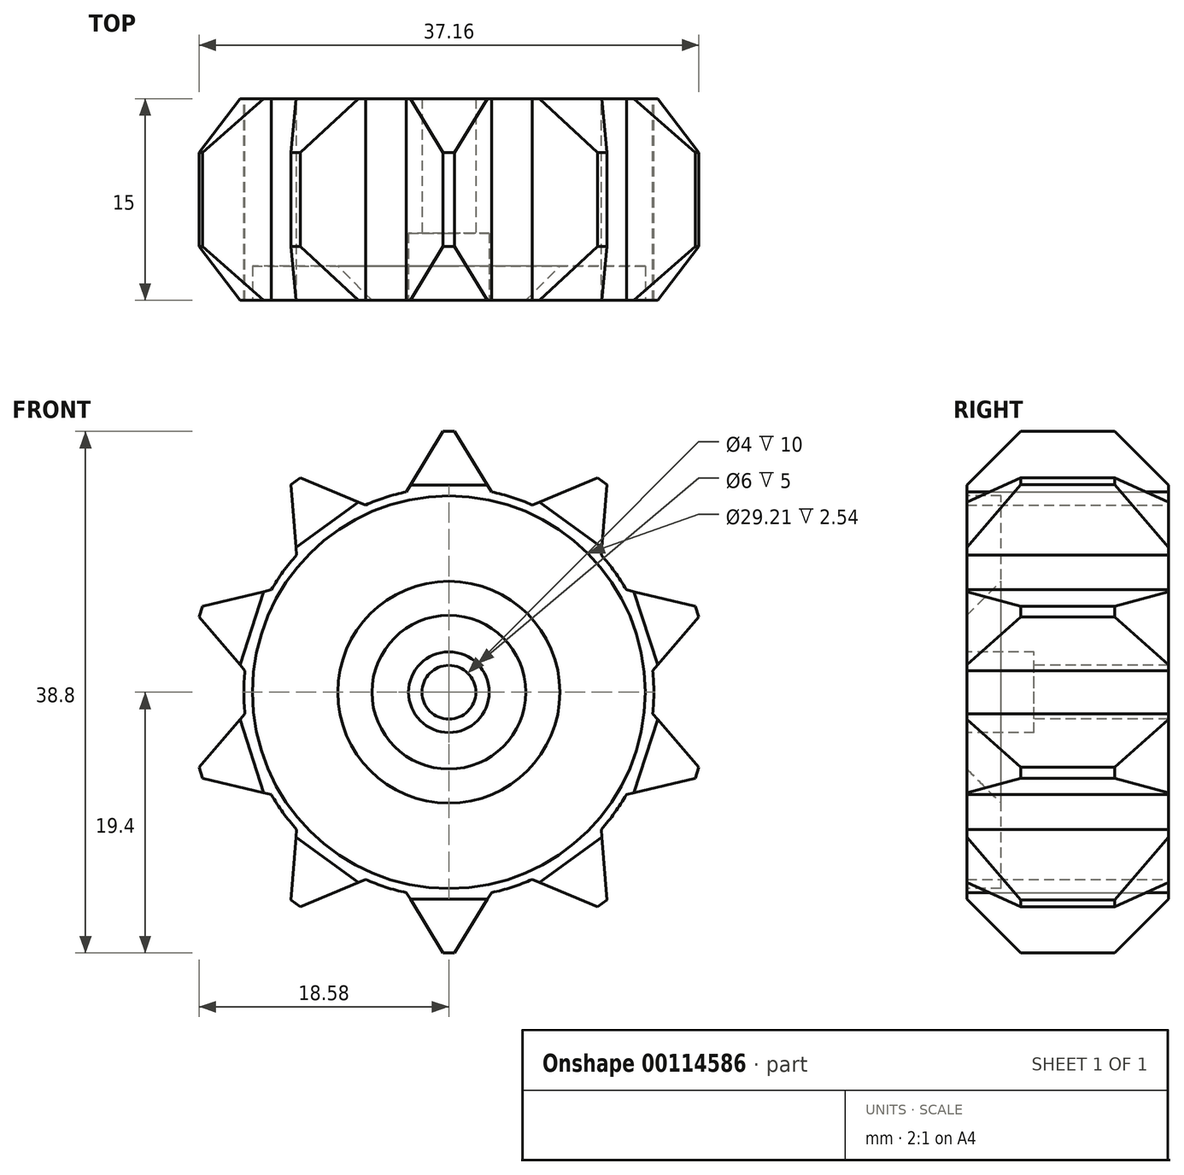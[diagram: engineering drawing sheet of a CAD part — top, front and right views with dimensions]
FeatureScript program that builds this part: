
annotation { "Feature Type Name" : "Feature", "Feature Type Description" : "" }
export const myFeature = defineFeature(function(context is Context, id is Id, definition is map)
    precondition{}
    {
        {
            var Q0;
            Q0=qCreatedBy(makeId("Front.planeOp"),FACE);
            var sketch = newSketch(context, id + "F0", { "sketchPlane" : qUnion([Q0])});
            skCircle(sketch, "E0", {"center": v(0, 0) * mm, "radius": 15.24 * mm});
            skLineSegment(sketch, "E1", {"start": v(0, 20.1) * mm, "end": v(3.17, 14.9) * mm});
            skLineSegment(sketch, "E2.MirrorCS", {"start": v(0, 20.1) * mm, "end": v(-3.17, 14.9) * mm});
            skLineSegment(sketch, "E3.1.0", {"start": v(-11.81, 16.26) * mm, "end": v(-11.32, 10.2) * mm});
            skLineSegment(sketch, "E3.1.1", {"start": v(-11.81, 16.26) * mm, "end": v(-6.2, 13.92) * mm});
            skLineSegment(sketch, "E3.2.0", {"start": v(-19.12, 6.21) * mm, "end": v(-15.16, 1.6) * mm});
            skLineSegment(sketch, "E3.2.1", {"start": v(-19.12, 6.21) * mm, "end": v(-13.2, 7.62) * mm});
            skLineSegment(sketch, "E4.2.3.0", {"start": v(-19.12, -6.21) * mm, "end": v(-13.2, -7.62) * mm});
            skLineSegment(sketch, "E4.3.3.0", {"start": v(-19.12, -6.21) * mm, "end": v(-15.16, -1.6) * mm});
            skLineSegment(sketch, "E4.2.4.0", {"start": v(-11.81, -16.26) * mm, "end": v(-6.2, -13.92) * mm});
            skLineSegment(sketch, "E4.3.4.0", {"start": v(-11.81, -16.26) * mm, "end": v(-11.32, -10.2) * mm});
            skLineSegment(sketch, "E4.2.5.0", {"start": v(0, -20.1) * mm, "end": v(3.17, -14.9) * mm});
            skLineSegment(sketch, "E4.3.5.0", {"start": v(0, -20.1) * mm, "end": v(-3.17, -14.9) * mm});
            skLineSegment(sketch, "E5.2.6.0", {"start": v(11.81, -16.26) * mm, "end": v(11.32, -10.2) * mm});
            skLineSegment(sketch, "E5.3.6.0", {"start": v(11.81, -16.26) * mm, "end": v(6.2, -13.92) * mm});
            skLineSegment(sketch, "E5.2.7.0", {"start": v(19.12, -6.21) * mm, "end": v(15.16, -1.6) * mm});
            skLineSegment(sketch, "E5.3.7.0", {"start": v(19.12, -6.21) * mm, "end": v(13.2, -7.62) * mm});
            skLineSegment(sketch, "E6.2.8.0", {"start": v(19.12, 6.21) * mm, "end": v(13.2, 7.62) * mm});
            skLineSegment(sketch, "E6.3.8.0", {"start": v(19.12, 6.21) * mm, "end": v(15.16, 1.6) * mm});
            skLineSegment(sketch, "E6.2.9.0", {"start": v(11.81, 16.26) * mm, "end": v(6.2, 13.92) * mm});
            skLineSegment(sketch, "E6.3.9.0", {"start": v(11.81, 16.26) * mm, "end": v(11.32, 10.2) * mm});
            skSolve(sketch);
        }
        {
            var Q0;
            {var subQ0=sQuery(id+"F0.wireOp",EDGE,"E4.2.5.0");Q0=makeQuery(id+"F0.imprint","IMPRINT",FACE,{"disambiguationData":[TD([[makeQuery(id+"F0.imprint","IMPRINT",EDGE,{"derivedFrom":subQ0}),1.0]])]});}
            var Q1;
            {var subQ0=sQuery(id+"F0.wireOp",EDGE,"E1");Q1=makeQuery(id+"F0.imprint","IMPRINT",FACE,{"disambiguationData":[TD([[makeQuery(id+"F0.imprint","IMPRINT",EDGE,{"derivedFrom":subQ0}),-1.0]])]});}
            var Q2;
            {var subQ0=sQuery(id+"F0.wireOp",EDGE,"E3.1.0");Q2=makeQuery(id+"F0.imprint","IMPRINT",FACE,{"disambiguationData":[TD([[makeQuery(id+"F0.imprint","IMPRINT",EDGE,{"derivedFrom":subQ0}),1.0]])]});}
            var Q3;
            {var subQ0=sQuery(id+"F0.wireOp",EDGE,"E3.2.0");Q3=makeQuery(id+"F0.imprint","IMPRINT",FACE,{"disambiguationData":[TD([[makeQuery(id+"F0.imprint","IMPRINT",EDGE,{"derivedFrom":subQ0}),1.0]])]});}
            var Q4;
            {var subQ0=sQuery(id+"F0.wireOp",EDGE,"E4.2.3.0");Q4=makeQuery(id+"F0.imprint","IMPRINT",FACE,{"disambiguationData":[TD([[makeQuery(id+"F0.imprint","IMPRINT",EDGE,{"derivedFrom":subQ0}),1.0]])]});}
            var Q5;
            {var subQ0=sQuery(id+"F0.wireOp",EDGE,"E4.2.4.0");Q5=makeQuery(id+"F0.imprint","IMPRINT",FACE,{"disambiguationData":[TD([[makeQuery(id+"F0.imprint","IMPRINT",EDGE,{"derivedFrom":subQ0}),1.0]])]});}
            var Q6;
            {var subQ0=sQuery(id+"F0.wireOp",EDGE,"E0");var subQ3=makeQuery(id+"F0.imprint","INTERSECT",VERTEX,{"derivedFrom":[subQ0,sQuery(id+"F0.wireOp",EDGE,"E4.2.5.0")]});Q6=makeQuery(id+"F0.imprint","IMPRINT",FACE,{"disambiguationData":[TD([[makeQuery(id+"F0.imprint","IMPRINT",EDGE,{"disambiguationData":[TD([[subQ3,1.0]])],"derivedFrom":subQ0}),1.0]])]});}
            var Q7;
            {var subQ0=sQuery(id+"F0.wireOp",EDGE,"E6.2.9.0");Q7=makeQuery(id+"F0.imprint","IMPRINT",FACE,{"disambiguationData":[TD([[makeQuery(id+"F0.imprint","IMPRINT",EDGE,{"derivedFrom":subQ0}),1.0]])]});}
            var Q8;
            {var subQ0=sQuery(id+"F0.wireOp",EDGE,"E6.2.8.0");Q8=makeQuery(id+"F0.imprint","IMPRINT",FACE,{"disambiguationData":[TD([[makeQuery(id+"F0.imprint","IMPRINT",EDGE,{"derivedFrom":subQ0}),1.0]])]});}
            var Q9;
            {var subQ0=sQuery(id+"F0.wireOp",EDGE,"E5.2.7.0");Q9=makeQuery(id+"F0.imprint","IMPRINT",FACE,{"disambiguationData":[TD([[makeQuery(id+"F0.imprint","IMPRINT",EDGE,{"derivedFrom":subQ0}),1.0]])]});}
            var Q10;
            {var subQ0=sQuery(id+"F0.wireOp",EDGE,"E5.2.6.0");Q10=makeQuery(id+"F0.imprint","IMPRINT",FACE,{"disambiguationData":[TD([[makeQuery(id+"F0.imprint","IMPRINT",EDGE,{"derivedFrom":subQ0}),1.0]])]});}
            extrude(context, id + "F1", {"entities" : qUnion([Q0, Q1, Q2, Q3, Q4, Q5, Q6, Q7, Q8, Q9, Q10]), "depth" : 15 * mm});
        }
        {
            var Q0;
            Q0=makeQuery(id+"F1.opExtrude","SWEPT_EDGE",EDGE,{"disambiguationData":[OSD([sQuery(id+"F0.wireOp",EDGE,"E4.2.5.0"),sQuery(id+"F0.wireOp",EDGE,"E4.3.5.0")])]});
            var Q1;
            Q1=makeQuery(id+"F1.opExtrude","SWEPT_EDGE",EDGE,{"disambiguationData":[OSD([sQuery(id+"F0.wireOp",EDGE,"E1"),sQuery(id+"F0.wireOp",EDGE,"E2.MirrorCS")])]});
            var Q2;
            Q2=makeQuery(id+"F1.opExtrude","SWEPT_EDGE",EDGE,{"disambiguationData":[OSD([sQuery(id+"F0.wireOp",EDGE,"E4.2.4.0"),sQuery(id+"F0.wireOp",EDGE,"E4.3.4.0")])]});
            var Q3;
            Q3=makeQuery(id+"F1.opExtrude","SWEPT_EDGE",EDGE,{"disambiguationData":[OSD([sQuery(id+"F0.wireOp",EDGE,"E4.2.3.0"),sQuery(id+"F0.wireOp",EDGE,"E4.3.3.0")])]});
            var Q4;
            Q4=makeQuery(id+"F1.opExtrude","SWEPT_EDGE",EDGE,{"disambiguationData":[OSD([sQuery(id+"F0.wireOp",EDGE,"E3.2.0"),sQuery(id+"F0.wireOp",EDGE,"E3.2.1")])]});
            var Q5;
            Q5=makeQuery(id+"F1.opExtrude","SWEPT_EDGE",EDGE,{"disambiguationData":[OSD([sQuery(id+"F0.wireOp",EDGE,"E3.1.0"),sQuery(id+"F0.wireOp",EDGE,"E3.1.1")])]});
            var Q6;
            Q6=makeQuery(id+"F1.opExtrude","SWEPT_EDGE",EDGE,{"disambiguationData":[OSD([sQuery(id+"F0.wireOp",EDGE,"E6.2.9.0"),sQuery(id+"F0.wireOp",EDGE,"E6.3.9.0")])]});
            var Q7;
            Q7=makeQuery(id+"F1.opExtrude","SWEPT_EDGE",EDGE,{"disambiguationData":[OSD([sQuery(id+"F0.wireOp",EDGE,"E6.2.8.0"),sQuery(id+"F0.wireOp",EDGE,"E6.3.8.0")])]});
            var Q8;
            Q8=makeQuery(id+"F1.opExtrude","SWEPT_EDGE",EDGE,{"disambiguationData":[OSD([sQuery(id+"F0.wireOp",EDGE,"E5.2.7.0"),sQuery(id+"F0.wireOp",EDGE,"E5.3.7.0")])]});
            var Q9;
            Q9=makeQuery(id+"F1.opExtrude","SWEPT_EDGE",EDGE,{"disambiguationData":[OSD([sQuery(id+"F0.wireOp",EDGE,"E5.2.6.0"),sQuery(id+"F0.wireOp",EDGE,"E5.3.6.0")])]});
            chamfer(context, id + "F2", {"entities" : qUnion([Q0, Q1, Q2, Q3, Q4, Q5, Q6, Q7, Q8, Q9]), "width" : .5 * mm, "tangentPropagation" : true});
        }
        {
            var Q0;
            {var subQ0=sQuery(id+"F0.wireOp",EDGE,"E3.1.1");var subQ1=sQuery(id+"F0.wireOp",EDGE,"E3.1.0");Q0=makeQuery(id+"F2.opChamfer","BLEND_EDGE",EDGE,{"blendedFrom":[makeQuery(id+"F1.opExtrude","SWEPT_EDGE",EDGE,{"disambiguationData":[OSD([subQ1,subQ0])]}),makeQuery(id+"F1.opExtrude","CAP_FACE",FACE,{"disambiguationData":[OSD([sQuery(id+"F0.wireOp",EDGE,"E0"),sQuery(id+"F0.wireOp",EDGE,"E1"),sQuery(id+"F0.wireOp",EDGE,"E2.MirrorCS"),subQ1,subQ0,sQuery(id+"F0.wireOp",EDGE,"E3.2.0"),sQuery(id+"F0.wireOp",EDGE,"E3.2.1"),sQuery(id+"F0.wireOp",EDGE,"E4.2.3.0"),sQuery(id+"F0.wireOp",EDGE,"E4.3.3.0"),sQuery(id+"F0.wireOp",EDGE,"E4.2.4.0"),sQuery(id+"F0.wireOp",EDGE,"E4.3.4.0"),sQuery(id+"F0.wireOp",EDGE,"E4.2.5.0"),sQuery(id+"F0.wireOp",EDGE,"E4.3.5.0")])],"isStart":false})],"blendedInto":[makeQuery(id+"F1.opExtrude","CAP_FACE",FACE,{"disambiguationData":[OSD([sQuery(id+"F0.wireOp",EDGE,"E0"),sQuery(id+"F0.wireOp",EDGE,"E1"),sQuery(id+"F0.wireOp",EDGE,"E2.MirrorCS"),subQ1,subQ0,sQuery(id+"F0.wireOp",EDGE,"E3.2.0"),sQuery(id+"F0.wireOp",EDGE,"E3.2.1"),sQuery(id+"F0.wireOp",EDGE,"E4.2.3.0"),sQuery(id+"F0.wireOp",EDGE,"E4.3.3.0"),sQuery(id+"F0.wireOp",EDGE,"E4.2.4.0"),sQuery(id+"F0.wireOp",EDGE,"E4.3.4.0"),sQuery(id+"F0.wireOp",EDGE,"E4.2.5.0"),sQuery(id+"F0.wireOp",EDGE,"E4.3.5.0")])],"isStart":false})]});}
            var Q1;
            {var subQ0=sQuery(id+"F0.wireOp",EDGE,"E3.1.1");var subQ1=sQuery(id+"F0.wireOp",EDGE,"E3.1.0");Q1=makeQuery(id+"F2.opChamfer","BLEND_EDGE",EDGE,{"blendedFrom":[makeQuery(id+"F1.opExtrude","SWEPT_EDGE",EDGE,{"disambiguationData":[OSD([subQ1,subQ0])]}),makeQuery(id+"F1.opExtrude","CAP_FACE",FACE,{"disambiguationData":[OSD([sQuery(id+"F0.wireOp",EDGE,"E0"),sQuery(id+"F0.wireOp",EDGE,"E1"),sQuery(id+"F0.wireOp",EDGE,"E2.MirrorCS"),subQ1,subQ0,sQuery(id+"F0.wireOp",EDGE,"E3.2.0"),sQuery(id+"F0.wireOp",EDGE,"E3.2.1"),sQuery(id+"F0.wireOp",EDGE,"E4.2.3.0"),sQuery(id+"F0.wireOp",EDGE,"E4.3.3.0"),sQuery(id+"F0.wireOp",EDGE,"E4.2.4.0"),sQuery(id+"F0.wireOp",EDGE,"E4.3.4.0"),sQuery(id+"F0.wireOp",EDGE,"E4.2.5.0"),sQuery(id+"F0.wireOp",EDGE,"E4.3.5.0")])],"isStart":true})],"blendedInto":[makeQuery(id+"F1.opExtrude","CAP_FACE",FACE,{"disambiguationData":[OSD([sQuery(id+"F0.wireOp",EDGE,"E0"),sQuery(id+"F0.wireOp",EDGE,"E1"),sQuery(id+"F0.wireOp",EDGE,"E2.MirrorCS"),subQ1,subQ0,sQuery(id+"F0.wireOp",EDGE,"E3.2.0"),sQuery(id+"F0.wireOp",EDGE,"E3.2.1"),sQuery(id+"F0.wireOp",EDGE,"E4.2.3.0"),sQuery(id+"F0.wireOp",EDGE,"E4.3.3.0"),sQuery(id+"F0.wireOp",EDGE,"E4.2.4.0"),sQuery(id+"F0.wireOp",EDGE,"E4.3.4.0"),sQuery(id+"F0.wireOp",EDGE,"E4.2.5.0"),sQuery(id+"F0.wireOp",EDGE,"E4.3.5.0")])],"isStart":true})]});}
            var Q2;
            {var subQ0=sQuery(id+"F0.wireOp",EDGE,"E2.MirrorCS");var subQ1=sQuery(id+"F0.wireOp",EDGE,"E1");Q2=makeQuery(id+"F2.opChamfer","BLEND_EDGE",EDGE,{"blendedFrom":[makeQuery(id+"F1.opExtrude","SWEPT_EDGE",EDGE,{"disambiguationData":[OSD([subQ1,subQ0])]}),makeQuery(id+"F1.opExtrude","CAP_FACE",FACE,{"disambiguationData":[OSD([sQuery(id+"F0.wireOp",EDGE,"E0"),subQ1,subQ0,sQuery(id+"F0.wireOp",EDGE,"E3.1.0"),sQuery(id+"F0.wireOp",EDGE,"E3.1.1"),sQuery(id+"F0.wireOp",EDGE,"E3.2.0"),sQuery(id+"F0.wireOp",EDGE,"E3.2.1"),sQuery(id+"F0.wireOp",EDGE,"E4.2.3.0"),sQuery(id+"F0.wireOp",EDGE,"E4.3.3.0"),sQuery(id+"F0.wireOp",EDGE,"E4.2.4.0"),sQuery(id+"F0.wireOp",EDGE,"E4.3.4.0"),sQuery(id+"F0.wireOp",EDGE,"E4.2.5.0"),sQuery(id+"F0.wireOp",EDGE,"E4.3.5.0")])],"isStart":true})],"blendedInto":[makeQuery(id+"F1.opExtrude","CAP_FACE",FACE,{"disambiguationData":[OSD([sQuery(id+"F0.wireOp",EDGE,"E0"),subQ1,subQ0,sQuery(id+"F0.wireOp",EDGE,"E3.1.0"),sQuery(id+"F0.wireOp",EDGE,"E3.1.1"),sQuery(id+"F0.wireOp",EDGE,"E3.2.0"),sQuery(id+"F0.wireOp",EDGE,"E3.2.1"),sQuery(id+"F0.wireOp",EDGE,"E4.2.3.0"),sQuery(id+"F0.wireOp",EDGE,"E4.3.3.0"),sQuery(id+"F0.wireOp",EDGE,"E4.2.4.0"),sQuery(id+"F0.wireOp",EDGE,"E4.3.4.0"),sQuery(id+"F0.wireOp",EDGE,"E4.2.5.0"),sQuery(id+"F0.wireOp",EDGE,"E4.3.5.0")])],"isStart":true})]});}
            var Q3;
            {var subQ0=sQuery(id+"F0.wireOp",EDGE,"E2.MirrorCS");var subQ1=sQuery(id+"F0.wireOp",EDGE,"E1");Q3=makeQuery(id+"F2.opChamfer","BLEND_EDGE",EDGE,{"blendedFrom":[makeQuery(id+"F1.opExtrude","SWEPT_EDGE",EDGE,{"disambiguationData":[OSD([subQ1,subQ0])]}),makeQuery(id+"F1.opExtrude","CAP_FACE",FACE,{"disambiguationData":[OSD([sQuery(id+"F0.wireOp",EDGE,"E0"),subQ1,subQ0,sQuery(id+"F0.wireOp",EDGE,"E3.1.0"),sQuery(id+"F0.wireOp",EDGE,"E3.1.1"),sQuery(id+"F0.wireOp",EDGE,"E3.2.0"),sQuery(id+"F0.wireOp",EDGE,"E3.2.1"),sQuery(id+"F0.wireOp",EDGE,"E4.2.3.0"),sQuery(id+"F0.wireOp",EDGE,"E4.3.3.0"),sQuery(id+"F0.wireOp",EDGE,"E4.2.4.0"),sQuery(id+"F0.wireOp",EDGE,"E4.3.4.0"),sQuery(id+"F0.wireOp",EDGE,"E4.2.5.0"),sQuery(id+"F0.wireOp",EDGE,"E4.3.5.0")])],"isStart":false})],"blendedInto":[makeQuery(id+"F1.opExtrude","CAP_FACE",FACE,{"disambiguationData":[OSD([sQuery(id+"F0.wireOp",EDGE,"E0"),subQ1,subQ0,sQuery(id+"F0.wireOp",EDGE,"E3.1.0"),sQuery(id+"F0.wireOp",EDGE,"E3.1.1"),sQuery(id+"F0.wireOp",EDGE,"E3.2.0"),sQuery(id+"F0.wireOp",EDGE,"E3.2.1"),sQuery(id+"F0.wireOp",EDGE,"E4.2.3.0"),sQuery(id+"F0.wireOp",EDGE,"E4.3.3.0"),sQuery(id+"F0.wireOp",EDGE,"E4.2.4.0"),sQuery(id+"F0.wireOp",EDGE,"E4.3.4.0"),sQuery(id+"F0.wireOp",EDGE,"E4.2.5.0"),sQuery(id+"F0.wireOp",EDGE,"E4.3.5.0")])],"isStart":false})]});}
            var Q4;
            {var subQ0=sQuery(id+"F0.wireOp",EDGE,"E4.3.5.0");var subQ1=sQuery(id+"F0.wireOp",EDGE,"E4.2.5.0");Q4=makeQuery(id+"F2.opChamfer","BLEND_EDGE",EDGE,{"blendedFrom":[makeQuery(id+"F1.opExtrude","SWEPT_EDGE",EDGE,{"disambiguationData":[OSD([subQ1,subQ0])]}),makeQuery(id+"F1.opExtrude","CAP_FACE",FACE,{"disambiguationData":[OSD([sQuery(id+"F0.wireOp",EDGE,"E0"),sQuery(id+"F0.wireOp",EDGE,"E1"),sQuery(id+"F0.wireOp",EDGE,"E2.MirrorCS"),sQuery(id+"F0.wireOp",EDGE,"E3.1.0"),sQuery(id+"F0.wireOp",EDGE,"E3.1.1"),sQuery(id+"F0.wireOp",EDGE,"E3.2.0"),sQuery(id+"F0.wireOp",EDGE,"E3.2.1"),sQuery(id+"F0.wireOp",EDGE,"E4.2.3.0"),sQuery(id+"F0.wireOp",EDGE,"E4.3.3.0"),sQuery(id+"F0.wireOp",EDGE,"E4.2.4.0"),sQuery(id+"F0.wireOp",EDGE,"E4.3.4.0"),subQ1,subQ0])],"isStart":false})],"blendedInto":[makeQuery(id+"F1.opExtrude","CAP_FACE",FACE,{"disambiguationData":[OSD([sQuery(id+"F0.wireOp",EDGE,"E0"),sQuery(id+"F0.wireOp",EDGE,"E1"),sQuery(id+"F0.wireOp",EDGE,"E2.MirrorCS"),sQuery(id+"F0.wireOp",EDGE,"E3.1.0"),sQuery(id+"F0.wireOp",EDGE,"E3.1.1"),sQuery(id+"F0.wireOp",EDGE,"E3.2.0"),sQuery(id+"F0.wireOp",EDGE,"E3.2.1"),sQuery(id+"F0.wireOp",EDGE,"E4.2.3.0"),sQuery(id+"F0.wireOp",EDGE,"E4.3.3.0"),sQuery(id+"F0.wireOp",EDGE,"E4.2.4.0"),sQuery(id+"F0.wireOp",EDGE,"E4.3.4.0"),subQ1,subQ0])],"isStart":false})]});}
            var Q5;
            {var subQ0=sQuery(id+"F0.wireOp",EDGE,"E4.3.4.0");var subQ1=sQuery(id+"F0.wireOp",EDGE,"E4.2.4.0");Q5=makeQuery(id+"F2.opChamfer","BLEND_EDGE",EDGE,{"blendedFrom":[makeQuery(id+"F1.opExtrude","SWEPT_EDGE",EDGE,{"disambiguationData":[OSD([subQ1,subQ0])]}),makeQuery(id+"F1.opExtrude","CAP_FACE",FACE,{"disambiguationData":[OSD([sQuery(id+"F0.wireOp",EDGE,"E0"),sQuery(id+"F0.wireOp",EDGE,"E1"),sQuery(id+"F0.wireOp",EDGE,"E2.MirrorCS"),sQuery(id+"F0.wireOp",EDGE,"E3.1.0"),sQuery(id+"F0.wireOp",EDGE,"E3.1.1"),sQuery(id+"F0.wireOp",EDGE,"E3.2.0"),sQuery(id+"F0.wireOp",EDGE,"E3.2.1"),sQuery(id+"F0.wireOp",EDGE,"E4.2.3.0"),sQuery(id+"F0.wireOp",EDGE,"E4.3.3.0"),subQ1,subQ0,sQuery(id+"F0.wireOp",EDGE,"E4.2.5.0"),sQuery(id+"F0.wireOp",EDGE,"E4.3.5.0")])],"isStart":false})],"blendedInto":[makeQuery(id+"F1.opExtrude","CAP_FACE",FACE,{"disambiguationData":[OSD([sQuery(id+"F0.wireOp",EDGE,"E0"),sQuery(id+"F0.wireOp",EDGE,"E1"),sQuery(id+"F0.wireOp",EDGE,"E2.MirrorCS"),sQuery(id+"F0.wireOp",EDGE,"E3.1.0"),sQuery(id+"F0.wireOp",EDGE,"E3.1.1"),sQuery(id+"F0.wireOp",EDGE,"E3.2.0"),sQuery(id+"F0.wireOp",EDGE,"E3.2.1"),sQuery(id+"F0.wireOp",EDGE,"E4.2.3.0"),sQuery(id+"F0.wireOp",EDGE,"E4.3.3.0"),subQ1,subQ0,sQuery(id+"F0.wireOp",EDGE,"E4.2.5.0"),sQuery(id+"F0.wireOp",EDGE,"E4.3.5.0")])],"isStart":false})]});}
            var Q6;
            {var subQ0=sQuery(id+"F0.wireOp",EDGE,"E4.3.3.0");var subQ1=sQuery(id+"F0.wireOp",EDGE,"E4.2.3.0");Q6=makeQuery(id+"F2.opChamfer","BLEND_EDGE",EDGE,{"blendedFrom":[makeQuery(id+"F1.opExtrude","SWEPT_EDGE",EDGE,{"disambiguationData":[OSD([subQ1,subQ0])]}),makeQuery(id+"F1.opExtrude","CAP_FACE",FACE,{"disambiguationData":[OSD([sQuery(id+"F0.wireOp",EDGE,"E0"),sQuery(id+"F0.wireOp",EDGE,"E1"),sQuery(id+"F0.wireOp",EDGE,"E2.MirrorCS"),sQuery(id+"F0.wireOp",EDGE,"E3.1.0"),sQuery(id+"F0.wireOp",EDGE,"E3.1.1"),sQuery(id+"F0.wireOp",EDGE,"E3.2.0"),sQuery(id+"F0.wireOp",EDGE,"E3.2.1"),subQ1,subQ0,sQuery(id+"F0.wireOp",EDGE,"E4.2.4.0"),sQuery(id+"F0.wireOp",EDGE,"E4.3.4.0"),sQuery(id+"F0.wireOp",EDGE,"E4.2.5.0"),sQuery(id+"F0.wireOp",EDGE,"E4.3.5.0")])],"isStart":false})],"blendedInto":[makeQuery(id+"F1.opExtrude","CAP_FACE",FACE,{"disambiguationData":[OSD([sQuery(id+"F0.wireOp",EDGE,"E0"),sQuery(id+"F0.wireOp",EDGE,"E1"),sQuery(id+"F0.wireOp",EDGE,"E2.MirrorCS"),sQuery(id+"F0.wireOp",EDGE,"E3.1.0"),sQuery(id+"F0.wireOp",EDGE,"E3.1.1"),sQuery(id+"F0.wireOp",EDGE,"E3.2.0"),sQuery(id+"F0.wireOp",EDGE,"E3.2.1"),subQ1,subQ0,sQuery(id+"F0.wireOp",EDGE,"E4.2.4.0"),sQuery(id+"F0.wireOp",EDGE,"E4.3.4.0"),sQuery(id+"F0.wireOp",EDGE,"E4.2.5.0"),sQuery(id+"F0.wireOp",EDGE,"E4.3.5.0")])],"isStart":false})]});}
            var Q7;
            {var subQ0=sQuery(id+"F0.wireOp",EDGE,"E3.2.1");var subQ1=sQuery(id+"F0.wireOp",EDGE,"E3.2.0");Q7=makeQuery(id+"F2.opChamfer","BLEND_EDGE",EDGE,{"blendedFrom":[makeQuery(id+"F1.opExtrude","SWEPT_EDGE",EDGE,{"disambiguationData":[OSD([subQ1,subQ0])]}),makeQuery(id+"F1.opExtrude","CAP_FACE",FACE,{"disambiguationData":[OSD([sQuery(id+"F0.wireOp",EDGE,"E0"),sQuery(id+"F0.wireOp",EDGE,"E1"),sQuery(id+"F0.wireOp",EDGE,"E2.MirrorCS"),sQuery(id+"F0.wireOp",EDGE,"E3.1.0"),sQuery(id+"F0.wireOp",EDGE,"E3.1.1"),subQ1,subQ0,sQuery(id+"F0.wireOp",EDGE,"E4.2.3.0"),sQuery(id+"F0.wireOp",EDGE,"E4.3.3.0"),sQuery(id+"F0.wireOp",EDGE,"E4.2.4.0"),sQuery(id+"F0.wireOp",EDGE,"E4.3.4.0"),sQuery(id+"F0.wireOp",EDGE,"E4.2.5.0"),sQuery(id+"F0.wireOp",EDGE,"E4.3.5.0")])],"isStart":false})],"blendedInto":[makeQuery(id+"F1.opExtrude","CAP_FACE",FACE,{"disambiguationData":[OSD([sQuery(id+"F0.wireOp",EDGE,"E0"),sQuery(id+"F0.wireOp",EDGE,"E1"),sQuery(id+"F0.wireOp",EDGE,"E2.MirrorCS"),sQuery(id+"F0.wireOp",EDGE,"E3.1.0"),sQuery(id+"F0.wireOp",EDGE,"E3.1.1"),subQ1,subQ0,sQuery(id+"F0.wireOp",EDGE,"E4.2.3.0"),sQuery(id+"F0.wireOp",EDGE,"E4.3.3.0"),sQuery(id+"F0.wireOp",EDGE,"E4.2.4.0"),sQuery(id+"F0.wireOp",EDGE,"E4.3.4.0"),sQuery(id+"F0.wireOp",EDGE,"E4.2.5.0"),sQuery(id+"F0.wireOp",EDGE,"E4.3.5.0")])],"isStart":false})]});}
            var Q8;
            {var subQ0=sQuery(id+"F0.wireOp",EDGE,"E3.2.1");var subQ1=sQuery(id+"F0.wireOp",EDGE,"E3.2.0");Q8=makeQuery(id+"F2.opChamfer","BLEND_EDGE",EDGE,{"blendedFrom":[makeQuery(id+"F1.opExtrude","SWEPT_EDGE",EDGE,{"disambiguationData":[OSD([subQ1,subQ0])]}),makeQuery(id+"F1.opExtrude","CAP_FACE",FACE,{"disambiguationData":[OSD([sQuery(id+"F0.wireOp",EDGE,"E0"),sQuery(id+"F0.wireOp",EDGE,"E1"),sQuery(id+"F0.wireOp",EDGE,"E2.MirrorCS"),sQuery(id+"F0.wireOp",EDGE,"E3.1.0"),sQuery(id+"F0.wireOp",EDGE,"E3.1.1"),subQ1,subQ0,sQuery(id+"F0.wireOp",EDGE,"E4.2.3.0"),sQuery(id+"F0.wireOp",EDGE,"E4.3.3.0"),sQuery(id+"F0.wireOp",EDGE,"E4.2.4.0"),sQuery(id+"F0.wireOp",EDGE,"E4.3.4.0"),sQuery(id+"F0.wireOp",EDGE,"E4.2.5.0"),sQuery(id+"F0.wireOp",EDGE,"E4.3.5.0")])],"isStart":true})],"blendedInto":[makeQuery(id+"F1.opExtrude","CAP_FACE",FACE,{"disambiguationData":[OSD([sQuery(id+"F0.wireOp",EDGE,"E0"),sQuery(id+"F0.wireOp",EDGE,"E1"),sQuery(id+"F0.wireOp",EDGE,"E2.MirrorCS"),sQuery(id+"F0.wireOp",EDGE,"E3.1.0"),sQuery(id+"F0.wireOp",EDGE,"E3.1.1"),subQ1,subQ0,sQuery(id+"F0.wireOp",EDGE,"E4.2.3.0"),sQuery(id+"F0.wireOp",EDGE,"E4.3.3.0"),sQuery(id+"F0.wireOp",EDGE,"E4.2.4.0"),sQuery(id+"F0.wireOp",EDGE,"E4.3.4.0"),sQuery(id+"F0.wireOp",EDGE,"E4.2.5.0"),sQuery(id+"F0.wireOp",EDGE,"E4.3.5.0")])],"isStart":true})]});}
            var Q9;
            {var subQ0=sQuery(id+"F0.wireOp",EDGE,"E4.3.3.0");var subQ1=sQuery(id+"F0.wireOp",EDGE,"E4.2.3.0");Q9=makeQuery(id+"F2.opChamfer","BLEND_EDGE",EDGE,{"blendedFrom":[makeQuery(id+"F1.opExtrude","SWEPT_EDGE",EDGE,{"disambiguationData":[OSD([subQ1,subQ0])]}),makeQuery(id+"F1.opExtrude","CAP_FACE",FACE,{"disambiguationData":[OSD([sQuery(id+"F0.wireOp",EDGE,"E0"),sQuery(id+"F0.wireOp",EDGE,"E1"),sQuery(id+"F0.wireOp",EDGE,"E2.MirrorCS"),sQuery(id+"F0.wireOp",EDGE,"E3.1.0"),sQuery(id+"F0.wireOp",EDGE,"E3.1.1"),sQuery(id+"F0.wireOp",EDGE,"E3.2.0"),sQuery(id+"F0.wireOp",EDGE,"E3.2.1"),subQ1,subQ0,sQuery(id+"F0.wireOp",EDGE,"E4.2.4.0"),sQuery(id+"F0.wireOp",EDGE,"E4.3.4.0"),sQuery(id+"F0.wireOp",EDGE,"E4.2.5.0"),sQuery(id+"F0.wireOp",EDGE,"E4.3.5.0")])],"isStart":true})],"blendedInto":[makeQuery(id+"F1.opExtrude","CAP_FACE",FACE,{"disambiguationData":[OSD([sQuery(id+"F0.wireOp",EDGE,"E0"),sQuery(id+"F0.wireOp",EDGE,"E1"),sQuery(id+"F0.wireOp",EDGE,"E2.MirrorCS"),sQuery(id+"F0.wireOp",EDGE,"E3.1.0"),sQuery(id+"F0.wireOp",EDGE,"E3.1.1"),sQuery(id+"F0.wireOp",EDGE,"E3.2.0"),sQuery(id+"F0.wireOp",EDGE,"E3.2.1"),subQ1,subQ0,sQuery(id+"F0.wireOp",EDGE,"E4.2.4.0"),sQuery(id+"F0.wireOp",EDGE,"E4.3.4.0"),sQuery(id+"F0.wireOp",EDGE,"E4.2.5.0"),sQuery(id+"F0.wireOp",EDGE,"E4.3.5.0")])],"isStart":true})]});}
            var Q10;
            {var subQ0=sQuery(id+"F0.wireOp",EDGE,"E4.3.4.0");var subQ1=sQuery(id+"F0.wireOp",EDGE,"E4.2.4.0");Q10=makeQuery(id+"F2.opChamfer","BLEND_EDGE",EDGE,{"blendedFrom":[makeQuery(id+"F1.opExtrude","SWEPT_EDGE",EDGE,{"disambiguationData":[OSD([subQ1,subQ0])]}),makeQuery(id+"F1.opExtrude","CAP_FACE",FACE,{"disambiguationData":[OSD([sQuery(id+"F0.wireOp",EDGE,"E0"),sQuery(id+"F0.wireOp",EDGE,"E1"),sQuery(id+"F0.wireOp",EDGE,"E2.MirrorCS"),sQuery(id+"F0.wireOp",EDGE,"E3.1.0"),sQuery(id+"F0.wireOp",EDGE,"E3.1.1"),sQuery(id+"F0.wireOp",EDGE,"E3.2.0"),sQuery(id+"F0.wireOp",EDGE,"E3.2.1"),sQuery(id+"F0.wireOp",EDGE,"E4.2.3.0"),sQuery(id+"F0.wireOp",EDGE,"E4.3.3.0"),subQ1,subQ0,sQuery(id+"F0.wireOp",EDGE,"E4.2.5.0"),sQuery(id+"F0.wireOp",EDGE,"E4.3.5.0")])],"isStart":true})],"blendedInto":[makeQuery(id+"F1.opExtrude","CAP_FACE",FACE,{"disambiguationData":[OSD([sQuery(id+"F0.wireOp",EDGE,"E0"),sQuery(id+"F0.wireOp",EDGE,"E1"),sQuery(id+"F0.wireOp",EDGE,"E2.MirrorCS"),sQuery(id+"F0.wireOp",EDGE,"E3.1.0"),sQuery(id+"F0.wireOp",EDGE,"E3.1.1"),sQuery(id+"F0.wireOp",EDGE,"E3.2.0"),sQuery(id+"F0.wireOp",EDGE,"E3.2.1"),sQuery(id+"F0.wireOp",EDGE,"E4.2.3.0"),sQuery(id+"F0.wireOp",EDGE,"E4.3.3.0"),subQ1,subQ0,sQuery(id+"F0.wireOp",EDGE,"E4.2.5.0"),sQuery(id+"F0.wireOp",EDGE,"E4.3.5.0")])],"isStart":true})]});}
            var Q11;
            {var subQ0=sQuery(id+"F0.wireOp",EDGE,"E4.3.5.0");var subQ1=sQuery(id+"F0.wireOp",EDGE,"E4.2.5.0");Q11=makeQuery(id+"F2.opChamfer","BLEND_EDGE",EDGE,{"blendedFrom":[makeQuery(id+"F1.opExtrude","SWEPT_EDGE",EDGE,{"disambiguationData":[OSD([subQ1,subQ0])]}),makeQuery(id+"F1.opExtrude","CAP_FACE",FACE,{"disambiguationData":[OSD([sQuery(id+"F0.wireOp",EDGE,"E0"),sQuery(id+"F0.wireOp",EDGE,"E1"),sQuery(id+"F0.wireOp",EDGE,"E2.MirrorCS"),sQuery(id+"F0.wireOp",EDGE,"E3.1.0"),sQuery(id+"F0.wireOp",EDGE,"E3.1.1"),sQuery(id+"F0.wireOp",EDGE,"E3.2.0"),sQuery(id+"F0.wireOp",EDGE,"E3.2.1"),sQuery(id+"F0.wireOp",EDGE,"E4.2.3.0"),sQuery(id+"F0.wireOp",EDGE,"E4.3.3.0"),sQuery(id+"F0.wireOp",EDGE,"E4.2.4.0"),sQuery(id+"F0.wireOp",EDGE,"E4.3.4.0"),subQ1,subQ0])],"isStart":true})],"blendedInto":[makeQuery(id+"F1.opExtrude","CAP_FACE",FACE,{"disambiguationData":[OSD([sQuery(id+"F0.wireOp",EDGE,"E0"),sQuery(id+"F0.wireOp",EDGE,"E1"),sQuery(id+"F0.wireOp",EDGE,"E2.MirrorCS"),sQuery(id+"F0.wireOp",EDGE,"E3.1.0"),sQuery(id+"F0.wireOp",EDGE,"E3.1.1"),sQuery(id+"F0.wireOp",EDGE,"E3.2.0"),sQuery(id+"F0.wireOp",EDGE,"E3.2.1"),sQuery(id+"F0.wireOp",EDGE,"E4.2.3.0"),sQuery(id+"F0.wireOp",EDGE,"E4.3.3.0"),sQuery(id+"F0.wireOp",EDGE,"E4.2.4.0"),sQuery(id+"F0.wireOp",EDGE,"E4.3.4.0"),subQ1,subQ0])],"isStart":true})]});}
            var Q12;
            {var subQ0=sQuery(id+"F0.wireOp",EDGE,"E6.3.9.0");var subQ1=sQuery(id+"F0.wireOp",EDGE,"E6.2.9.0");Q12=makeQuery(id+"F2.opChamfer","BLEND_EDGE",EDGE,{"blendedFrom":[makeQuery(id+"F1.opExtrude","SWEPT_EDGE",EDGE,{"disambiguationData":[OSD([subQ1,subQ0])]}),makeQuery(id+"F1.opExtrude","CAP_FACE",FACE,{"disambiguationData":[OSD([sQuery(id+"F0.wireOp",EDGE,"E0"),sQuery(id+"F0.wireOp",EDGE,"E1"),sQuery(id+"F0.wireOp",EDGE,"E2.MirrorCS"),sQuery(id+"F0.wireOp",EDGE,"E3.1.0"),sQuery(id+"F0.wireOp",EDGE,"E3.1.1"),sQuery(id+"F0.wireOp",EDGE,"E3.2.0"),sQuery(id+"F0.wireOp",EDGE,"E3.2.1"),sQuery(id+"F0.wireOp",EDGE,"E4.2.3.0"),sQuery(id+"F0.wireOp",EDGE,"E4.3.3.0"),sQuery(id+"F0.wireOp",EDGE,"E4.2.4.0"),sQuery(id+"F0.wireOp",EDGE,"E4.3.4.0"),sQuery(id+"F0.wireOp",EDGE,"E4.2.5.0"),sQuery(id+"F0.wireOp",EDGE,"E4.3.5.0"),sQuery(id+"F0.wireOp",EDGE,"E5.2.6.0"),sQuery(id+"F0.wireOp",EDGE,"E5.3.6.0"),sQuery(id+"F0.wireOp",EDGE,"E5.2.7.0"),sQuery(id+"F0.wireOp",EDGE,"E5.3.7.0"),sQuery(id+"F0.wireOp",EDGE,"E6.2.8.0"),sQuery(id+"F0.wireOp",EDGE,"E6.3.8.0"),subQ1,subQ0])],"isStart":false})],"blendedInto":[makeQuery(id+"F1.opExtrude","CAP_FACE",FACE,{"disambiguationData":[OSD([sQuery(id+"F0.wireOp",EDGE,"E0"),sQuery(id+"F0.wireOp",EDGE,"E1"),sQuery(id+"F0.wireOp",EDGE,"E2.MirrorCS"),sQuery(id+"F0.wireOp",EDGE,"E3.1.0"),sQuery(id+"F0.wireOp",EDGE,"E3.1.1"),sQuery(id+"F0.wireOp",EDGE,"E3.2.0"),sQuery(id+"F0.wireOp",EDGE,"E3.2.1"),sQuery(id+"F0.wireOp",EDGE,"E4.2.3.0"),sQuery(id+"F0.wireOp",EDGE,"E4.3.3.0"),sQuery(id+"F0.wireOp",EDGE,"E4.2.4.0"),sQuery(id+"F0.wireOp",EDGE,"E4.3.4.0"),sQuery(id+"F0.wireOp",EDGE,"E4.2.5.0"),sQuery(id+"F0.wireOp",EDGE,"E4.3.5.0"),sQuery(id+"F0.wireOp",EDGE,"E5.2.6.0"),sQuery(id+"F0.wireOp",EDGE,"E5.3.6.0"),sQuery(id+"F0.wireOp",EDGE,"E5.2.7.0"),sQuery(id+"F0.wireOp",EDGE,"E5.3.7.0"),sQuery(id+"F0.wireOp",EDGE,"E6.2.8.0"),sQuery(id+"F0.wireOp",EDGE,"E6.3.8.0"),subQ1,subQ0])],"isStart":false})]});}
            var Q13;
            {var subQ0=sQuery(id+"F0.wireOp",EDGE,"E6.3.8.0");var subQ1=sQuery(id+"F0.wireOp",EDGE,"E6.2.8.0");Q13=makeQuery(id+"F2.opChamfer","BLEND_EDGE",EDGE,{"blendedFrom":[makeQuery(id+"F1.opExtrude","SWEPT_EDGE",EDGE,{"disambiguationData":[OSD([subQ1,subQ0])]}),makeQuery(id+"F1.opExtrude","CAP_FACE",FACE,{"disambiguationData":[OSD([sQuery(id+"F0.wireOp",EDGE,"E0"),sQuery(id+"F0.wireOp",EDGE,"E1"),sQuery(id+"F0.wireOp",EDGE,"E2.MirrorCS"),sQuery(id+"F0.wireOp",EDGE,"E3.1.0"),sQuery(id+"F0.wireOp",EDGE,"E3.1.1"),sQuery(id+"F0.wireOp",EDGE,"E3.2.0"),sQuery(id+"F0.wireOp",EDGE,"E3.2.1"),sQuery(id+"F0.wireOp",EDGE,"E4.2.3.0"),sQuery(id+"F0.wireOp",EDGE,"E4.3.3.0"),sQuery(id+"F0.wireOp",EDGE,"E4.2.4.0"),sQuery(id+"F0.wireOp",EDGE,"E4.3.4.0"),sQuery(id+"F0.wireOp",EDGE,"E4.2.5.0"),sQuery(id+"F0.wireOp",EDGE,"E4.3.5.0"),sQuery(id+"F0.wireOp",EDGE,"E5.2.6.0"),sQuery(id+"F0.wireOp",EDGE,"E5.3.6.0"),sQuery(id+"F0.wireOp",EDGE,"E5.2.7.0"),sQuery(id+"F0.wireOp",EDGE,"E5.3.7.0"),subQ1,subQ0,sQuery(id+"F0.wireOp",EDGE,"E6.2.9.0"),sQuery(id+"F0.wireOp",EDGE,"E6.3.9.0")])],"isStart":false})],"blendedInto":[makeQuery(id+"F1.opExtrude","CAP_FACE",FACE,{"disambiguationData":[OSD([sQuery(id+"F0.wireOp",EDGE,"E0"),sQuery(id+"F0.wireOp",EDGE,"E1"),sQuery(id+"F0.wireOp",EDGE,"E2.MirrorCS"),sQuery(id+"F0.wireOp",EDGE,"E3.1.0"),sQuery(id+"F0.wireOp",EDGE,"E3.1.1"),sQuery(id+"F0.wireOp",EDGE,"E3.2.0"),sQuery(id+"F0.wireOp",EDGE,"E3.2.1"),sQuery(id+"F0.wireOp",EDGE,"E4.2.3.0"),sQuery(id+"F0.wireOp",EDGE,"E4.3.3.0"),sQuery(id+"F0.wireOp",EDGE,"E4.2.4.0"),sQuery(id+"F0.wireOp",EDGE,"E4.3.4.0"),sQuery(id+"F0.wireOp",EDGE,"E4.2.5.0"),sQuery(id+"F0.wireOp",EDGE,"E4.3.5.0"),sQuery(id+"F0.wireOp",EDGE,"E5.2.6.0"),sQuery(id+"F0.wireOp",EDGE,"E5.3.6.0"),sQuery(id+"F0.wireOp",EDGE,"E5.2.7.0"),sQuery(id+"F0.wireOp",EDGE,"E5.3.7.0"),subQ1,subQ0,sQuery(id+"F0.wireOp",EDGE,"E6.2.9.0"),sQuery(id+"F0.wireOp",EDGE,"E6.3.9.0")])],"isStart":false})]});}
            var Q14;
            {var subQ0=sQuery(id+"F0.wireOp",EDGE,"E5.3.7.0");var subQ1=sQuery(id+"F0.wireOp",EDGE,"E5.2.7.0");Q14=makeQuery(id+"F2.opChamfer","BLEND_EDGE",EDGE,{"blendedFrom":[makeQuery(id+"F1.opExtrude","SWEPT_EDGE",EDGE,{"disambiguationData":[OSD([subQ1,subQ0])]}),makeQuery(id+"F1.opExtrude","CAP_FACE",FACE,{"disambiguationData":[OSD([sQuery(id+"F0.wireOp",EDGE,"E0"),sQuery(id+"F0.wireOp",EDGE,"E1"),sQuery(id+"F0.wireOp",EDGE,"E2.MirrorCS"),sQuery(id+"F0.wireOp",EDGE,"E3.1.0"),sQuery(id+"F0.wireOp",EDGE,"E3.1.1"),sQuery(id+"F0.wireOp",EDGE,"E3.2.0"),sQuery(id+"F0.wireOp",EDGE,"E3.2.1"),sQuery(id+"F0.wireOp",EDGE,"E4.2.3.0"),sQuery(id+"F0.wireOp",EDGE,"E4.3.3.0"),sQuery(id+"F0.wireOp",EDGE,"E4.2.4.0"),sQuery(id+"F0.wireOp",EDGE,"E4.3.4.0"),sQuery(id+"F0.wireOp",EDGE,"E4.2.5.0"),sQuery(id+"F0.wireOp",EDGE,"E4.3.5.0"),sQuery(id+"F0.wireOp",EDGE,"E5.2.6.0"),sQuery(id+"F0.wireOp",EDGE,"E5.3.6.0"),subQ1,subQ0,sQuery(id+"F0.wireOp",EDGE,"E6.2.8.0"),sQuery(id+"F0.wireOp",EDGE,"E6.3.8.0"),sQuery(id+"F0.wireOp",EDGE,"E6.2.9.0"),sQuery(id+"F0.wireOp",EDGE,"E6.3.9.0")])],"isStart":false})],"blendedInto":[makeQuery(id+"F1.opExtrude","CAP_FACE",FACE,{"disambiguationData":[OSD([sQuery(id+"F0.wireOp",EDGE,"E0"),sQuery(id+"F0.wireOp",EDGE,"E1"),sQuery(id+"F0.wireOp",EDGE,"E2.MirrorCS"),sQuery(id+"F0.wireOp",EDGE,"E3.1.0"),sQuery(id+"F0.wireOp",EDGE,"E3.1.1"),sQuery(id+"F0.wireOp",EDGE,"E3.2.0"),sQuery(id+"F0.wireOp",EDGE,"E3.2.1"),sQuery(id+"F0.wireOp",EDGE,"E4.2.3.0"),sQuery(id+"F0.wireOp",EDGE,"E4.3.3.0"),sQuery(id+"F0.wireOp",EDGE,"E4.2.4.0"),sQuery(id+"F0.wireOp",EDGE,"E4.3.4.0"),sQuery(id+"F0.wireOp",EDGE,"E4.2.5.0"),sQuery(id+"F0.wireOp",EDGE,"E4.3.5.0"),sQuery(id+"F0.wireOp",EDGE,"E5.2.6.0"),sQuery(id+"F0.wireOp",EDGE,"E5.3.6.0"),subQ1,subQ0,sQuery(id+"F0.wireOp",EDGE,"E6.2.8.0"),sQuery(id+"F0.wireOp",EDGE,"E6.3.8.0"),sQuery(id+"F0.wireOp",EDGE,"E6.2.9.0"),sQuery(id+"F0.wireOp",EDGE,"E6.3.9.0")])],"isStart":false})]});}
            var Q15;
            {var subQ0=sQuery(id+"F0.wireOp",EDGE,"E5.3.6.0");var subQ1=sQuery(id+"F0.wireOp",EDGE,"E5.2.6.0");Q15=makeQuery(id+"F2.opChamfer","BLEND_EDGE",EDGE,{"blendedFrom":[makeQuery(id+"F1.opExtrude","SWEPT_EDGE",EDGE,{"disambiguationData":[OSD([subQ1,subQ0])]}),makeQuery(id+"F1.opExtrude","CAP_FACE",FACE,{"disambiguationData":[OSD([sQuery(id+"F0.wireOp",EDGE,"E0"),sQuery(id+"F0.wireOp",EDGE,"E1"),sQuery(id+"F0.wireOp",EDGE,"E2.MirrorCS"),sQuery(id+"F0.wireOp",EDGE,"E3.1.0"),sQuery(id+"F0.wireOp",EDGE,"E3.1.1"),sQuery(id+"F0.wireOp",EDGE,"E3.2.0"),sQuery(id+"F0.wireOp",EDGE,"E3.2.1"),sQuery(id+"F0.wireOp",EDGE,"E4.2.3.0"),sQuery(id+"F0.wireOp",EDGE,"E4.3.3.0"),sQuery(id+"F0.wireOp",EDGE,"E4.2.4.0"),sQuery(id+"F0.wireOp",EDGE,"E4.3.4.0"),sQuery(id+"F0.wireOp",EDGE,"E4.2.5.0"),sQuery(id+"F0.wireOp",EDGE,"E4.3.5.0"),subQ1,subQ0,sQuery(id+"F0.wireOp",EDGE,"E5.2.7.0"),sQuery(id+"F0.wireOp",EDGE,"E5.3.7.0"),sQuery(id+"F0.wireOp",EDGE,"E6.2.8.0"),sQuery(id+"F0.wireOp",EDGE,"E6.3.8.0"),sQuery(id+"F0.wireOp",EDGE,"E6.2.9.0"),sQuery(id+"F0.wireOp",EDGE,"E6.3.9.0")])],"isStart":false})],"blendedInto":[makeQuery(id+"F1.opExtrude","CAP_FACE",FACE,{"disambiguationData":[OSD([sQuery(id+"F0.wireOp",EDGE,"E0"),sQuery(id+"F0.wireOp",EDGE,"E1"),sQuery(id+"F0.wireOp",EDGE,"E2.MirrorCS"),sQuery(id+"F0.wireOp",EDGE,"E3.1.0"),sQuery(id+"F0.wireOp",EDGE,"E3.1.1"),sQuery(id+"F0.wireOp",EDGE,"E3.2.0"),sQuery(id+"F0.wireOp",EDGE,"E3.2.1"),sQuery(id+"F0.wireOp",EDGE,"E4.2.3.0"),sQuery(id+"F0.wireOp",EDGE,"E4.3.3.0"),sQuery(id+"F0.wireOp",EDGE,"E4.2.4.0"),sQuery(id+"F0.wireOp",EDGE,"E4.3.4.0"),sQuery(id+"F0.wireOp",EDGE,"E4.2.5.0"),sQuery(id+"F0.wireOp",EDGE,"E4.3.5.0"),subQ1,subQ0,sQuery(id+"F0.wireOp",EDGE,"E5.2.7.0"),sQuery(id+"F0.wireOp",EDGE,"E5.3.7.0"),sQuery(id+"F0.wireOp",EDGE,"E6.2.8.0"),sQuery(id+"F0.wireOp",EDGE,"E6.3.8.0"),sQuery(id+"F0.wireOp",EDGE,"E6.2.9.0"),sQuery(id+"F0.wireOp",EDGE,"E6.3.9.0")])],"isStart":false})]});}
            var Q16;
            {var subQ0=sQuery(id+"F0.wireOp",EDGE,"E6.3.9.0");var subQ1=sQuery(id+"F0.wireOp",EDGE,"E6.2.9.0");Q16=makeQuery(id+"F2.opChamfer","BLEND_EDGE",EDGE,{"blendedFrom":[makeQuery(id+"F1.opExtrude","SWEPT_EDGE",EDGE,{"disambiguationData":[OSD([subQ1,subQ0])]}),makeQuery(id+"F1.opExtrude","CAP_FACE",FACE,{"disambiguationData":[OSD([sQuery(id+"F0.wireOp",EDGE,"E0"),sQuery(id+"F0.wireOp",EDGE,"E1"),sQuery(id+"F0.wireOp",EDGE,"E2.MirrorCS"),sQuery(id+"F0.wireOp",EDGE,"E3.1.0"),sQuery(id+"F0.wireOp",EDGE,"E3.1.1"),sQuery(id+"F0.wireOp",EDGE,"E3.2.0"),sQuery(id+"F0.wireOp",EDGE,"E3.2.1"),sQuery(id+"F0.wireOp",EDGE,"E4.2.3.0"),sQuery(id+"F0.wireOp",EDGE,"E4.3.3.0"),sQuery(id+"F0.wireOp",EDGE,"E4.2.4.0"),sQuery(id+"F0.wireOp",EDGE,"E4.3.4.0"),sQuery(id+"F0.wireOp",EDGE,"E4.2.5.0"),sQuery(id+"F0.wireOp",EDGE,"E4.3.5.0"),sQuery(id+"F0.wireOp",EDGE,"E5.2.6.0"),sQuery(id+"F0.wireOp",EDGE,"E5.3.6.0"),sQuery(id+"F0.wireOp",EDGE,"E5.2.7.0"),sQuery(id+"F0.wireOp",EDGE,"E5.3.7.0"),sQuery(id+"F0.wireOp",EDGE,"E6.2.8.0"),sQuery(id+"F0.wireOp",EDGE,"E6.3.8.0"),subQ1,subQ0])],"isStart":true})],"blendedInto":[makeQuery(id+"F1.opExtrude","CAP_FACE",FACE,{"disambiguationData":[OSD([sQuery(id+"F0.wireOp",EDGE,"E0"),sQuery(id+"F0.wireOp",EDGE,"E1"),sQuery(id+"F0.wireOp",EDGE,"E2.MirrorCS"),sQuery(id+"F0.wireOp",EDGE,"E3.1.0"),sQuery(id+"F0.wireOp",EDGE,"E3.1.1"),sQuery(id+"F0.wireOp",EDGE,"E3.2.0"),sQuery(id+"F0.wireOp",EDGE,"E3.2.1"),sQuery(id+"F0.wireOp",EDGE,"E4.2.3.0"),sQuery(id+"F0.wireOp",EDGE,"E4.3.3.0"),sQuery(id+"F0.wireOp",EDGE,"E4.2.4.0"),sQuery(id+"F0.wireOp",EDGE,"E4.3.4.0"),sQuery(id+"F0.wireOp",EDGE,"E4.2.5.0"),sQuery(id+"F0.wireOp",EDGE,"E4.3.5.0"),sQuery(id+"F0.wireOp",EDGE,"E5.2.6.0"),sQuery(id+"F0.wireOp",EDGE,"E5.3.6.0"),sQuery(id+"F0.wireOp",EDGE,"E5.2.7.0"),sQuery(id+"F0.wireOp",EDGE,"E5.3.7.0"),sQuery(id+"F0.wireOp",EDGE,"E6.2.8.0"),sQuery(id+"F0.wireOp",EDGE,"E6.3.8.0"),subQ1,subQ0])],"isStart":true})]});}
            var Q17;
            {var subQ0=sQuery(id+"F0.wireOp",EDGE,"E6.3.8.0");var subQ1=sQuery(id+"F0.wireOp",EDGE,"E6.2.8.0");Q17=makeQuery(id+"F2.opChamfer","BLEND_EDGE",EDGE,{"blendedFrom":[makeQuery(id+"F1.opExtrude","SWEPT_EDGE",EDGE,{"disambiguationData":[OSD([subQ1,subQ0])]}),makeQuery(id+"F1.opExtrude","CAP_FACE",FACE,{"disambiguationData":[OSD([sQuery(id+"F0.wireOp",EDGE,"E0"),sQuery(id+"F0.wireOp",EDGE,"E1"),sQuery(id+"F0.wireOp",EDGE,"E2.MirrorCS"),sQuery(id+"F0.wireOp",EDGE,"E3.1.0"),sQuery(id+"F0.wireOp",EDGE,"E3.1.1"),sQuery(id+"F0.wireOp",EDGE,"E3.2.0"),sQuery(id+"F0.wireOp",EDGE,"E3.2.1"),sQuery(id+"F0.wireOp",EDGE,"E4.2.3.0"),sQuery(id+"F0.wireOp",EDGE,"E4.3.3.0"),sQuery(id+"F0.wireOp",EDGE,"E4.2.4.0"),sQuery(id+"F0.wireOp",EDGE,"E4.3.4.0"),sQuery(id+"F0.wireOp",EDGE,"E4.2.5.0"),sQuery(id+"F0.wireOp",EDGE,"E4.3.5.0"),sQuery(id+"F0.wireOp",EDGE,"E5.2.6.0"),sQuery(id+"F0.wireOp",EDGE,"E5.3.6.0"),sQuery(id+"F0.wireOp",EDGE,"E5.2.7.0"),sQuery(id+"F0.wireOp",EDGE,"E5.3.7.0"),subQ1,subQ0,sQuery(id+"F0.wireOp",EDGE,"E6.2.9.0"),sQuery(id+"F0.wireOp",EDGE,"E6.3.9.0")])],"isStart":true})],"blendedInto":[makeQuery(id+"F1.opExtrude","CAP_FACE",FACE,{"disambiguationData":[OSD([sQuery(id+"F0.wireOp",EDGE,"E0"),sQuery(id+"F0.wireOp",EDGE,"E1"),sQuery(id+"F0.wireOp",EDGE,"E2.MirrorCS"),sQuery(id+"F0.wireOp",EDGE,"E3.1.0"),sQuery(id+"F0.wireOp",EDGE,"E3.1.1"),sQuery(id+"F0.wireOp",EDGE,"E3.2.0"),sQuery(id+"F0.wireOp",EDGE,"E3.2.1"),sQuery(id+"F0.wireOp",EDGE,"E4.2.3.0"),sQuery(id+"F0.wireOp",EDGE,"E4.3.3.0"),sQuery(id+"F0.wireOp",EDGE,"E4.2.4.0"),sQuery(id+"F0.wireOp",EDGE,"E4.3.4.0"),sQuery(id+"F0.wireOp",EDGE,"E4.2.5.0"),sQuery(id+"F0.wireOp",EDGE,"E4.3.5.0"),sQuery(id+"F0.wireOp",EDGE,"E5.2.6.0"),sQuery(id+"F0.wireOp",EDGE,"E5.3.6.0"),sQuery(id+"F0.wireOp",EDGE,"E5.2.7.0"),sQuery(id+"F0.wireOp",EDGE,"E5.3.7.0"),subQ1,subQ0,sQuery(id+"F0.wireOp",EDGE,"E6.2.9.0"),sQuery(id+"F0.wireOp",EDGE,"E6.3.9.0")])],"isStart":true})]});}
            var Q18;
            {var subQ0=sQuery(id+"F0.wireOp",EDGE,"E5.3.7.0");var subQ1=sQuery(id+"F0.wireOp",EDGE,"E5.2.7.0");Q18=makeQuery(id+"F2.opChamfer","BLEND_EDGE",EDGE,{"blendedFrom":[makeQuery(id+"F1.opExtrude","SWEPT_EDGE",EDGE,{"disambiguationData":[OSD([subQ1,subQ0])]}),makeQuery(id+"F1.opExtrude","CAP_FACE",FACE,{"disambiguationData":[OSD([sQuery(id+"F0.wireOp",EDGE,"E0"),sQuery(id+"F0.wireOp",EDGE,"E1"),sQuery(id+"F0.wireOp",EDGE,"E2.MirrorCS"),sQuery(id+"F0.wireOp",EDGE,"E3.1.0"),sQuery(id+"F0.wireOp",EDGE,"E3.1.1"),sQuery(id+"F0.wireOp",EDGE,"E3.2.0"),sQuery(id+"F0.wireOp",EDGE,"E3.2.1"),sQuery(id+"F0.wireOp",EDGE,"E4.2.3.0"),sQuery(id+"F0.wireOp",EDGE,"E4.3.3.0"),sQuery(id+"F0.wireOp",EDGE,"E4.2.4.0"),sQuery(id+"F0.wireOp",EDGE,"E4.3.4.0"),sQuery(id+"F0.wireOp",EDGE,"E4.2.5.0"),sQuery(id+"F0.wireOp",EDGE,"E4.3.5.0"),sQuery(id+"F0.wireOp",EDGE,"E5.2.6.0"),sQuery(id+"F0.wireOp",EDGE,"E5.3.6.0"),subQ1,subQ0,sQuery(id+"F0.wireOp",EDGE,"E6.2.8.0"),sQuery(id+"F0.wireOp",EDGE,"E6.3.8.0"),sQuery(id+"F0.wireOp",EDGE,"E6.2.9.0"),sQuery(id+"F0.wireOp",EDGE,"E6.3.9.0")])],"isStart":true})],"blendedInto":[makeQuery(id+"F1.opExtrude","CAP_FACE",FACE,{"disambiguationData":[OSD([sQuery(id+"F0.wireOp",EDGE,"E0"),sQuery(id+"F0.wireOp",EDGE,"E1"),sQuery(id+"F0.wireOp",EDGE,"E2.MirrorCS"),sQuery(id+"F0.wireOp",EDGE,"E3.1.0"),sQuery(id+"F0.wireOp",EDGE,"E3.1.1"),sQuery(id+"F0.wireOp",EDGE,"E3.2.0"),sQuery(id+"F0.wireOp",EDGE,"E3.2.1"),sQuery(id+"F0.wireOp",EDGE,"E4.2.3.0"),sQuery(id+"F0.wireOp",EDGE,"E4.3.3.0"),sQuery(id+"F0.wireOp",EDGE,"E4.2.4.0"),sQuery(id+"F0.wireOp",EDGE,"E4.3.4.0"),sQuery(id+"F0.wireOp",EDGE,"E4.2.5.0"),sQuery(id+"F0.wireOp",EDGE,"E4.3.5.0"),sQuery(id+"F0.wireOp",EDGE,"E5.2.6.0"),sQuery(id+"F0.wireOp",EDGE,"E5.3.6.0"),subQ1,subQ0,sQuery(id+"F0.wireOp",EDGE,"E6.2.8.0"),sQuery(id+"F0.wireOp",EDGE,"E6.3.8.0"),sQuery(id+"F0.wireOp",EDGE,"E6.2.9.0"),sQuery(id+"F0.wireOp",EDGE,"E6.3.9.0")])],"isStart":true})]});}
            var Q19;
            {var subQ0=sQuery(id+"F0.wireOp",EDGE,"E5.3.6.0");var subQ1=sQuery(id+"F0.wireOp",EDGE,"E5.2.6.0");Q19=makeQuery(id+"F2.opChamfer","BLEND_EDGE",EDGE,{"blendedFrom":[makeQuery(id+"F1.opExtrude","SWEPT_EDGE",EDGE,{"disambiguationData":[OSD([subQ1,subQ0])]}),makeQuery(id+"F1.opExtrude","CAP_FACE",FACE,{"disambiguationData":[OSD([sQuery(id+"F0.wireOp",EDGE,"E0"),sQuery(id+"F0.wireOp",EDGE,"E1"),sQuery(id+"F0.wireOp",EDGE,"E2.MirrorCS"),sQuery(id+"F0.wireOp",EDGE,"E3.1.0"),sQuery(id+"F0.wireOp",EDGE,"E3.1.1"),sQuery(id+"F0.wireOp",EDGE,"E3.2.0"),sQuery(id+"F0.wireOp",EDGE,"E3.2.1"),sQuery(id+"F0.wireOp",EDGE,"E4.2.3.0"),sQuery(id+"F0.wireOp",EDGE,"E4.3.3.0"),sQuery(id+"F0.wireOp",EDGE,"E4.2.4.0"),sQuery(id+"F0.wireOp",EDGE,"E4.3.4.0"),sQuery(id+"F0.wireOp",EDGE,"E4.2.5.0"),sQuery(id+"F0.wireOp",EDGE,"E4.3.5.0"),subQ1,subQ0,sQuery(id+"F0.wireOp",EDGE,"E5.2.7.0"),sQuery(id+"F0.wireOp",EDGE,"E5.3.7.0"),sQuery(id+"F0.wireOp",EDGE,"E6.2.8.0"),sQuery(id+"F0.wireOp",EDGE,"E6.3.8.0"),sQuery(id+"F0.wireOp",EDGE,"E6.2.9.0"),sQuery(id+"F0.wireOp",EDGE,"E6.3.9.0")])],"isStart":true})],"blendedInto":[makeQuery(id+"F1.opExtrude","CAP_FACE",FACE,{"disambiguationData":[OSD([sQuery(id+"F0.wireOp",EDGE,"E0"),sQuery(id+"F0.wireOp",EDGE,"E1"),sQuery(id+"F0.wireOp",EDGE,"E2.MirrorCS"),sQuery(id+"F0.wireOp",EDGE,"E3.1.0"),sQuery(id+"F0.wireOp",EDGE,"E3.1.1"),sQuery(id+"F0.wireOp",EDGE,"E3.2.0"),sQuery(id+"F0.wireOp",EDGE,"E3.2.1"),sQuery(id+"F0.wireOp",EDGE,"E4.2.3.0"),sQuery(id+"F0.wireOp",EDGE,"E4.3.3.0"),sQuery(id+"F0.wireOp",EDGE,"E4.2.4.0"),sQuery(id+"F0.wireOp",EDGE,"E4.3.4.0"),sQuery(id+"F0.wireOp",EDGE,"E4.2.5.0"),sQuery(id+"F0.wireOp",EDGE,"E4.3.5.0"),subQ1,subQ0,sQuery(id+"F0.wireOp",EDGE,"E5.2.7.0"),sQuery(id+"F0.wireOp",EDGE,"E5.3.7.0"),sQuery(id+"F0.wireOp",EDGE,"E6.2.8.0"),sQuery(id+"F0.wireOp",EDGE,"E6.3.8.0"),sQuery(id+"F0.wireOp",EDGE,"E6.2.9.0"),sQuery(id+"F0.wireOp",EDGE,"E6.3.9.0")])],"isStart":true})]});}
            chamfer(context, id + "F3", {"entities" : qUnion([Q0, Q1, Q2, Q3, Q4, Q5, Q6, Q7, Q8, Q9, Q10, Q11, Q12, Q13, Q14, Q15, Q16, Q17, Q18, Q19]), "width" : 4 * mm, "tangentPropagation" : true});
        }
        {
            var Q0;
            Q0=makeQuery(id+"F1.opExtrude","CAP_FACE",FACE,{"disambiguationData":[OSD([sQuery(id+"F0.wireOp",EDGE,"E0"),sQuery(id+"F0.wireOp",EDGE,"E1"),sQuery(id+"F0.wireOp",EDGE,"E2.MirrorCS"),sQuery(id+"F0.wireOp",EDGE,"E3.1.0"),sQuery(id+"F0.wireOp",EDGE,"E3.1.1"),sQuery(id+"F0.wireOp",EDGE,"E3.2.0"),sQuery(id+"F0.wireOp",EDGE,"E3.2.1"),sQuery(id+"F0.wireOp",EDGE,"E4.2.3.0"),sQuery(id+"F0.wireOp",EDGE,"E4.3.3.0"),sQuery(id+"F0.wireOp",EDGE,"E4.2.4.0"),sQuery(id+"F0.wireOp",EDGE,"E4.3.4.0"),sQuery(id+"F0.wireOp",EDGE,"E4.2.5.0"),sQuery(id+"F0.wireOp",EDGE,"E4.3.5.0"),sQuery(id+"F0.wireOp",EDGE,"E5.2.6.0"),sQuery(id+"F0.wireOp",EDGE,"E5.3.6.0"),sQuery(id+"F0.wireOp",EDGE,"E5.2.7.0"),sQuery(id+"F0.wireOp",EDGE,"E5.3.7.0"),sQuery(id+"F0.wireOp",EDGE,"E6.2.8.0"),sQuery(id+"F0.wireOp",EDGE,"E6.3.8.0"),sQuery(id+"F0.wireOp",EDGE,"E6.2.9.0"),sQuery(id+"F0.wireOp",EDGE,"E6.3.9.0")])],"isStart":false});
            var sketch = newSketch(context, id + "F4", { "sketchPlane" : qUnion([Q0])});
            skCircle(sketch, "E7", {"center": v(0, 0) * mm, "radius": 2 * mm});
            skSolve(sketch);
        }
        {
            var Q0;
            Q0=qSketchRegion(id+"F4",true);
            extrude(context, id + "F5", {"entities" : qUnion([Q0]), "operationType" : NewBodyOperationType.REMOVE, "oppositeDirection" : true, "depth" : 25.4 * mm});
        }
        {
            var Q0;
            Q0=makeQuery(id+"F1.opExtrude","CAP_FACE",FACE,{"disambiguationData":[OSD([sQuery(id+"F0.wireOp",EDGE,"E0"),sQuery(id+"F0.wireOp",EDGE,"E1"),sQuery(id+"F0.wireOp",EDGE,"E2.MirrorCS"),sQuery(id+"F0.wireOp",EDGE,"E3.1.0"),sQuery(id+"F0.wireOp",EDGE,"E3.1.1"),sQuery(id+"F0.wireOp",EDGE,"E3.2.0"),sQuery(id+"F0.wireOp",EDGE,"E3.2.1"),sQuery(id+"F0.wireOp",EDGE,"E4.2.3.0"),sQuery(id+"F0.wireOp",EDGE,"E4.3.3.0"),sQuery(id+"F0.wireOp",EDGE,"E4.2.4.0"),sQuery(id+"F0.wireOp",EDGE,"E4.3.4.0"),sQuery(id+"F0.wireOp",EDGE,"E4.2.5.0"),sQuery(id+"F0.wireOp",EDGE,"E4.3.5.0"),sQuery(id+"F0.wireOp",EDGE,"E5.2.6.0"),sQuery(id+"F0.wireOp",EDGE,"E5.3.6.0"),sQuery(id+"F0.wireOp",EDGE,"E5.2.7.0"),sQuery(id+"F0.wireOp",EDGE,"E5.3.7.0"),sQuery(id+"F0.wireOp",EDGE,"E6.2.8.0"),sQuery(id+"F0.wireOp",EDGE,"E6.3.8.0"),sQuery(id+"F0.wireOp",EDGE,"E6.2.9.0"),sQuery(id+"F0.wireOp",EDGE,"E6.3.9.0")])],"isStart":false});
            var sketch = newSketch(context, id + "F6", { "sketchPlane" : qUnion([Q0])});
            skCircle(sketch, "E8", {"center": v(0, 0) * mm, "radius": 3 * mm});
            skSolve(sketch);
        }
        {
            var Q0;
            Q0=qSketchRegion(id+"F6",true);
            extrude(context, id + "F7", {"entities" : qUnion([Q0]), "operationType" : NewBodyOperationType.REMOVE, "oppositeDirection" : true, "depth" : 5 * mm});
        }
        {
            var Q0;
            Q0=makeQuery(id+"F1.opExtrude","CAP_FACE",FACE,{"disambiguationData":[OSD([sQuery(id+"F0.wireOp",EDGE,"E0"),sQuery(id+"F0.wireOp",EDGE,"E1"),sQuery(id+"F0.wireOp",EDGE,"E2.MirrorCS"),sQuery(id+"F0.wireOp",EDGE,"E3.1.0"),sQuery(id+"F0.wireOp",EDGE,"E3.1.1"),sQuery(id+"F0.wireOp",EDGE,"E3.2.0"),sQuery(id+"F0.wireOp",EDGE,"E3.2.1"),sQuery(id+"F0.wireOp",EDGE,"E4.2.3.0"),sQuery(id+"F0.wireOp",EDGE,"E4.3.3.0"),sQuery(id+"F0.wireOp",EDGE,"E4.2.4.0"),sQuery(id+"F0.wireOp",EDGE,"E4.3.4.0"),sQuery(id+"F0.wireOp",EDGE,"E4.2.5.0"),sQuery(id+"F0.wireOp",EDGE,"E4.3.5.0"),sQuery(id+"F0.wireOp",EDGE,"E5.2.6.0"),sQuery(id+"F0.wireOp",EDGE,"E5.3.6.0"),sQuery(id+"F0.wireOp",EDGE,"E5.2.7.0"),sQuery(id+"F0.wireOp",EDGE,"E5.3.7.0"),sQuery(id+"F0.wireOp",EDGE,"E6.2.8.0"),sQuery(id+"F0.wireOp",EDGE,"E6.3.8.0"),sQuery(id+"F0.wireOp",EDGE,"E6.2.9.0"),sQuery(id+"F0.wireOp",EDGE,"E6.3.9.0")])],"isStart":false});
            var sketch = newSketch(context, id + "F8", { "sketchPlane" : qUnion([Q0])});
            skCircle(sketch, "E9", {"center": v(0, 0) * mm, "radius": 3.18 * mm});
            skCircle(sketch, "E10", {"center": v(0, 0) * mm, "radius": 14.6 * mm});
            skSolve(sketch);
        }
        {
            var Q0;
            Q0=qSketchRegion(id+"F8",true);
            extrude(context, id + "F9", {"entities" : qUnion([Q0]), "operationType" : NewBodyOperationType.REMOVE, "oppositeDirection" : true, "depth" : 2.54 * mm});
        }
        {
            var Q0;
            Q0=makeQuery(id+"F9.boolean.opBoolean","COPY",EDGE,{"derivedFrom":makeQuery(id+"F9.opExtrude","CAP_EDGE",EDGE,{"disambiguationData":[OSD([sQuery(id+"F8.wireOp",EDGE,"E9")])],"isStart":false})});
            chamfer(context, id + "F10", {"entities" : qUnion([Q0]), "width" : 5.08 * mm, "tangentPropagation" : true});
        }
    });
